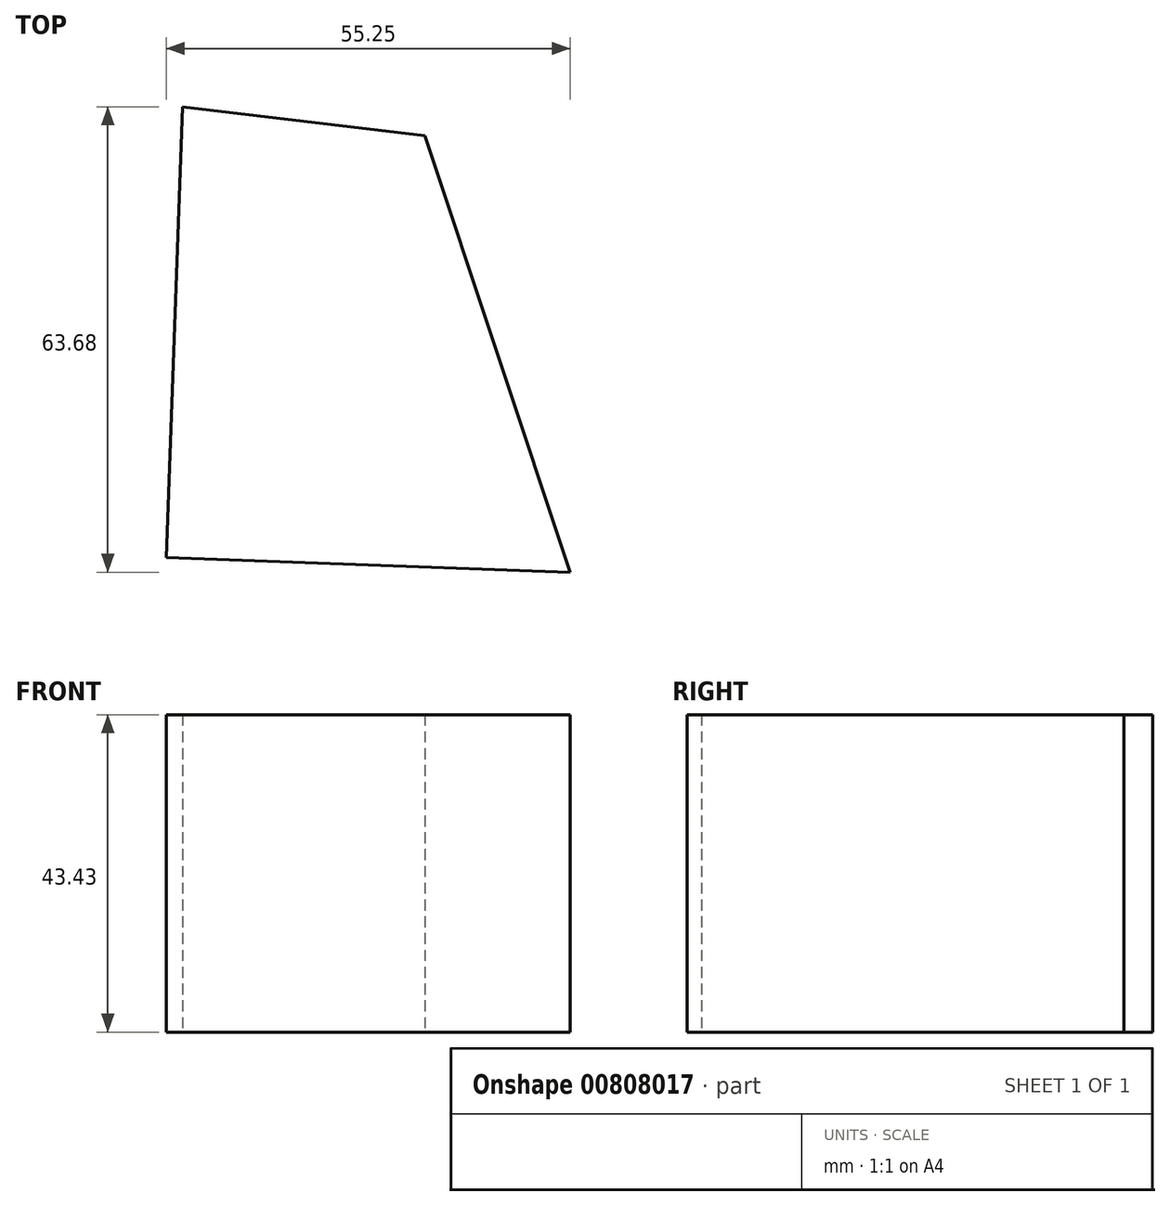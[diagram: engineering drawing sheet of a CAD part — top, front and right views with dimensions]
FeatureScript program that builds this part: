
annotation { "Feature Type Name" : "Feature", "Feature Type Description" : "" }
export const myFeature = defineFeature(function(context is Context, id is Id, definition is map)
    precondition{}
    {
        {
            var Q0;
            Q0=qCreatedBy(makeId("Top.planeOp"),FACE);
            var sketch = newSketch(context, id + "F0", { "sketchPlane" : qUnion([Q0])});
            skLineSegment(sketch, "E0", {"start": v(-35.27, 36.63) * mm, "end": v(-37.49, -25.07) * mm});
            skLineSegment(sketch, "E1", {"start": v(-37.49, -25.07) * mm, "end": v(17.76, -27.05) * mm});
            skLineSegment(sketch, "E2", {"start": v(17.76, -27.05) * mm, "end": v(-2.09, 32.7) * mm});
            skLineSegment(sketch, "E3", {"start": v(-2.09, 32.7) * mm, "end": v(-35.27, 36.63) * mm});
            skSolve(sketch);
        }
        {
            var Q0;
            Q0 = qSketchRegion(id + "F0", true);
            extrude(context, id + "F1", {"entities" : qUnion([Q0]), "depth" : 43.43 * mm, "offsetDistance" : 25.4 * mm});
        }
    });
